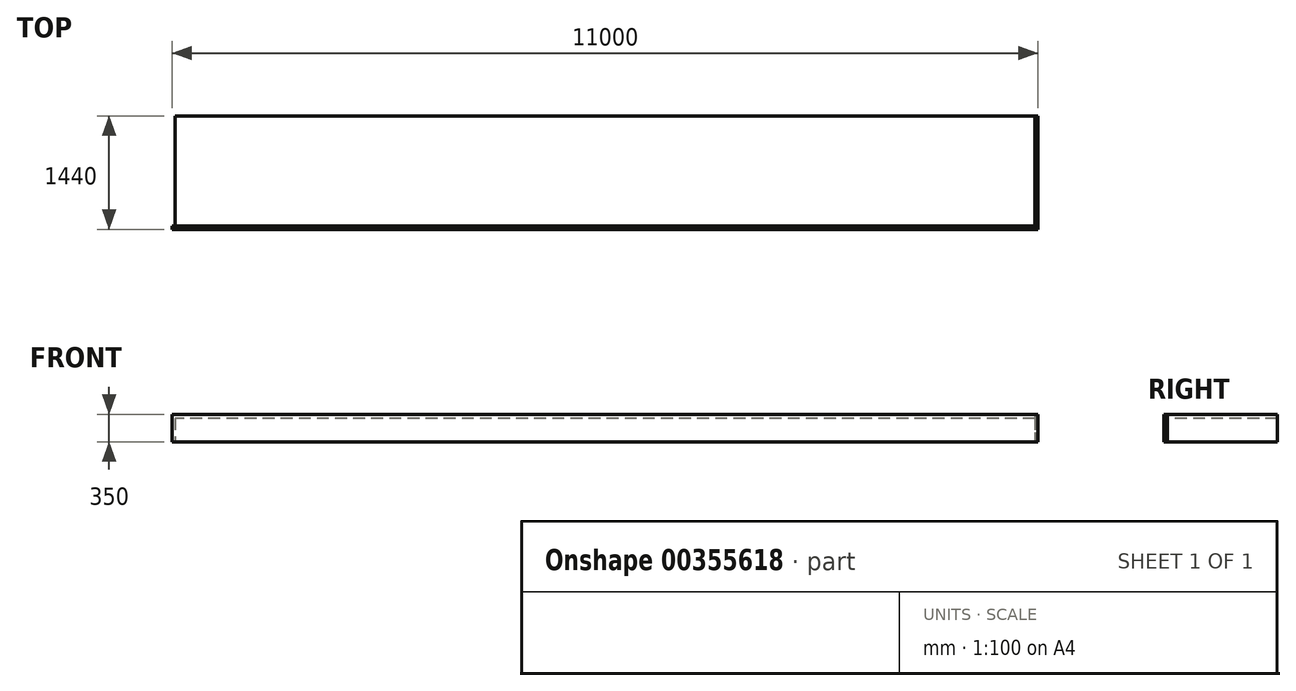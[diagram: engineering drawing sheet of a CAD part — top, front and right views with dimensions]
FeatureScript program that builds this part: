
annotation { "Feature Type Name" : "Feature", "Feature Type Description" : "" }
export const myFeature = defineFeature(function(context is Context, id is Id, definition is map)
    precondition{}
    {
        {
            var Q0;
            Q0=qCreatedBy(makeId("Top.planeOp"),FACE);
            var sketch = newSketch(context, id + "F0", { "sketchPlane" : qUnion([Q0])});
            skLineSegment(sketch, "E0.bottom", {"start": v(5460, 700) * mm, "end": v(-5460, 700) * mm});
            skLineSegment(sketch, "E0.top", {"start": v(5460, -700) * mm, "end": v(-5460, -700) * mm});
            skLineSegment(sketch, "E0.left", {"start": v(5460, 700) * mm, "end": v(5460, -700) * mm});
            skLineSegment(sketch, "E0.right", {"start": v(-5460, 700) * mm, "end": v(-5460, -700) * mm});
            skPoint(sketch, "E0.middle", {"position": v(0, 0) * mm});
            skSolve(sketch);
        }
        {
            var Q0;
            Q0=qSketchRegion(id+"F0",true);
            extrude(context, id + "F1", {"entities" : qUnion([Q0]), "depth" : 300 * mm});
        }
        {
            var Q0;
            Q0=makeQuery(id+"F1.opExtrude","SWEPT_FACE",FACE,{"disambiguationData":[OSD([sQuery(id+"F0.wireOp",EDGE,"E0.left")])]});
            var sketch = newSketch(context, id + "F2", { "sketchPlane" : qUnion([Q0])});
            skLineSegment(sketch, "E1.bottom", {"start": v(-700, 0) * mm, "end": v(700, 0) * mm});
            skLineSegment(sketch, "E1.top", {"start": v(-700, 350) * mm, "end": v(700, 350) * mm});
            skLineSegment(sketch, "E1.left", {"start": v(-700, 0) * mm, "end": v(-700, 350) * mm});
            skLineSegment(sketch, "E1.right", {"start": v(700, 0) * mm, "end": v(700, 350) * mm});
            skSolve(sketch);
        }
        {
            var Q0;
            Q0=qSketchRegion(id+"F2",true);
            extrude(context, id + "F3", {"entities" : qUnion([Q0]), "depth" : 40 * mm});
        }
        {
            var Q0;
            Q0=makeQuery(id+"F1.opExtrude","SWEPT_FACE",FACE,{"disambiguationData":[OSD([sQuery(id+"F0.wireOp",EDGE,"E0.top")])]});
            var sketch = newSketch(context, id + "F4", { "sketchPlane" : qUnion([Q0])});
            skLineSegment(sketch, "E2.bottom", {"start": v(-5500, 350) * mm, "end": v(5500, 350) * mm});
            skLineSegment(sketch, "E2.top", {"start": v(-5500, 0) * mm, "end": v(5500, 0) * mm});
            skLineSegment(sketch, "E2.left", {"start": v(-5500, 350) * mm, "end": v(-5500, 0) * mm});
            skLineSegment(sketch, "E2.right", {"start": v(5500, 350) * mm, "end": v(5500, 0) * mm});
            skSolve(sketch);
        }
        {
            var Q0;
            Q0=qSketchRegion(id+"F4",true);
            extrude(context, id + "F5", {"entities" : qUnion([Q0]), "depth" : 40 * mm});
        }
    });
